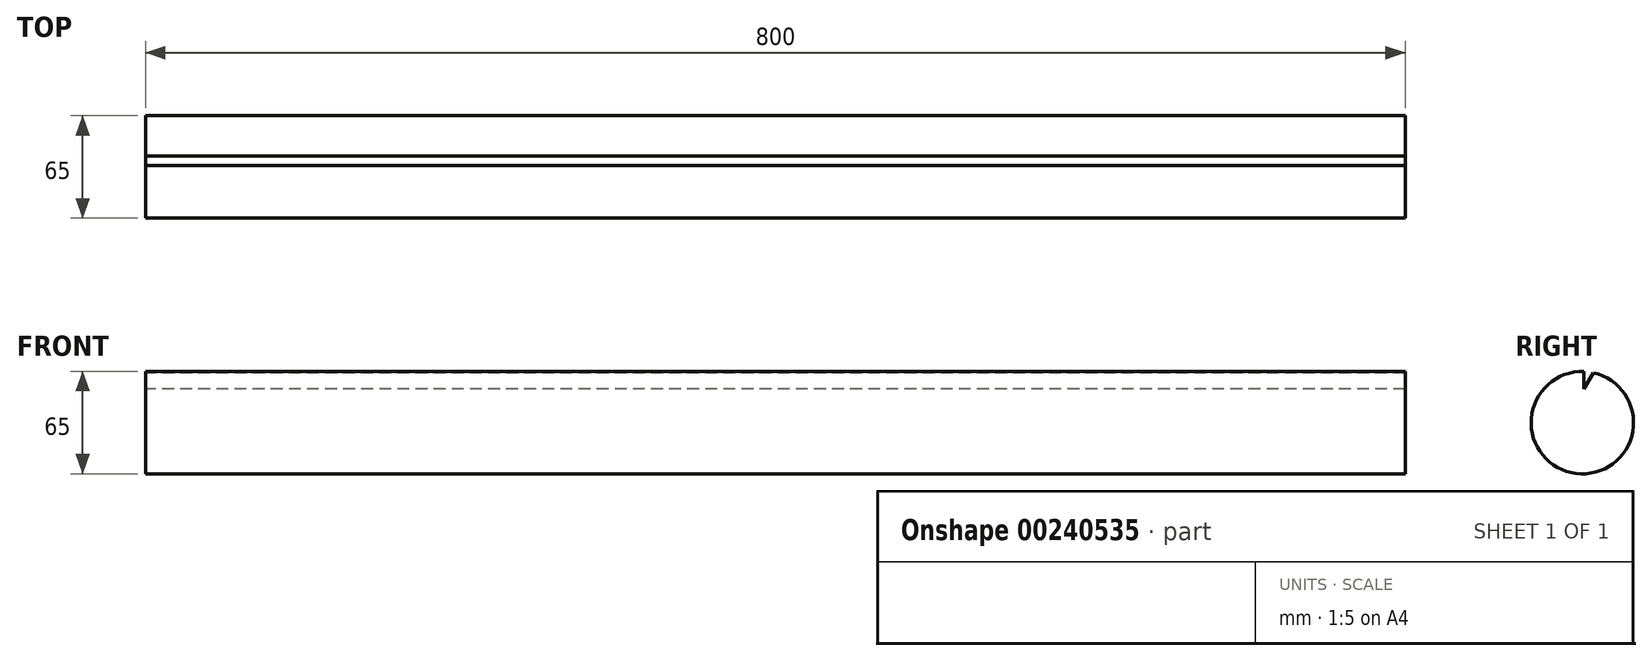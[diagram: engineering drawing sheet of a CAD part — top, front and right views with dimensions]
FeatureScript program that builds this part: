
annotation { "Feature Type Name" : "Feature", "Feature Type Description" : "" }
export const myFeature = defineFeature(function(context is Context, id is Id, definition is map)
    precondition{}
    {
        {
            var Q0;
            Q0=qCreatedBy(makeId("Right.planeOp"),FACE);
            var sketch = newSketch(context, id + "F0", { "sketchPlane" : qUnion([Q0])});
            skArc(sketch, "E0", {"start": v(-0.12, 32.25) * mm, "mid": v(-5.14, -32.48) * mm, "end": v(5.9, 31.5) * mm});
            skLineSegment(sketch, "E1", {"start": v(-0.12, 32.25) * mm, "end": v(-0.12, 21.3) * mm});
            skLineSegment(sketch, "E2", {"start": v(-0.12, 21.3) * mm, "end": v(5.9, 31.5) * mm});
            skSolve(sketch);
        }
        {
            var Q0;
            Q0 = qSketchRegion(id + "F0", true);
            extrude(context, id + "F1", {"entities" : qUnion([Q0]), "depth" : 800 * mm});
        }
    });
